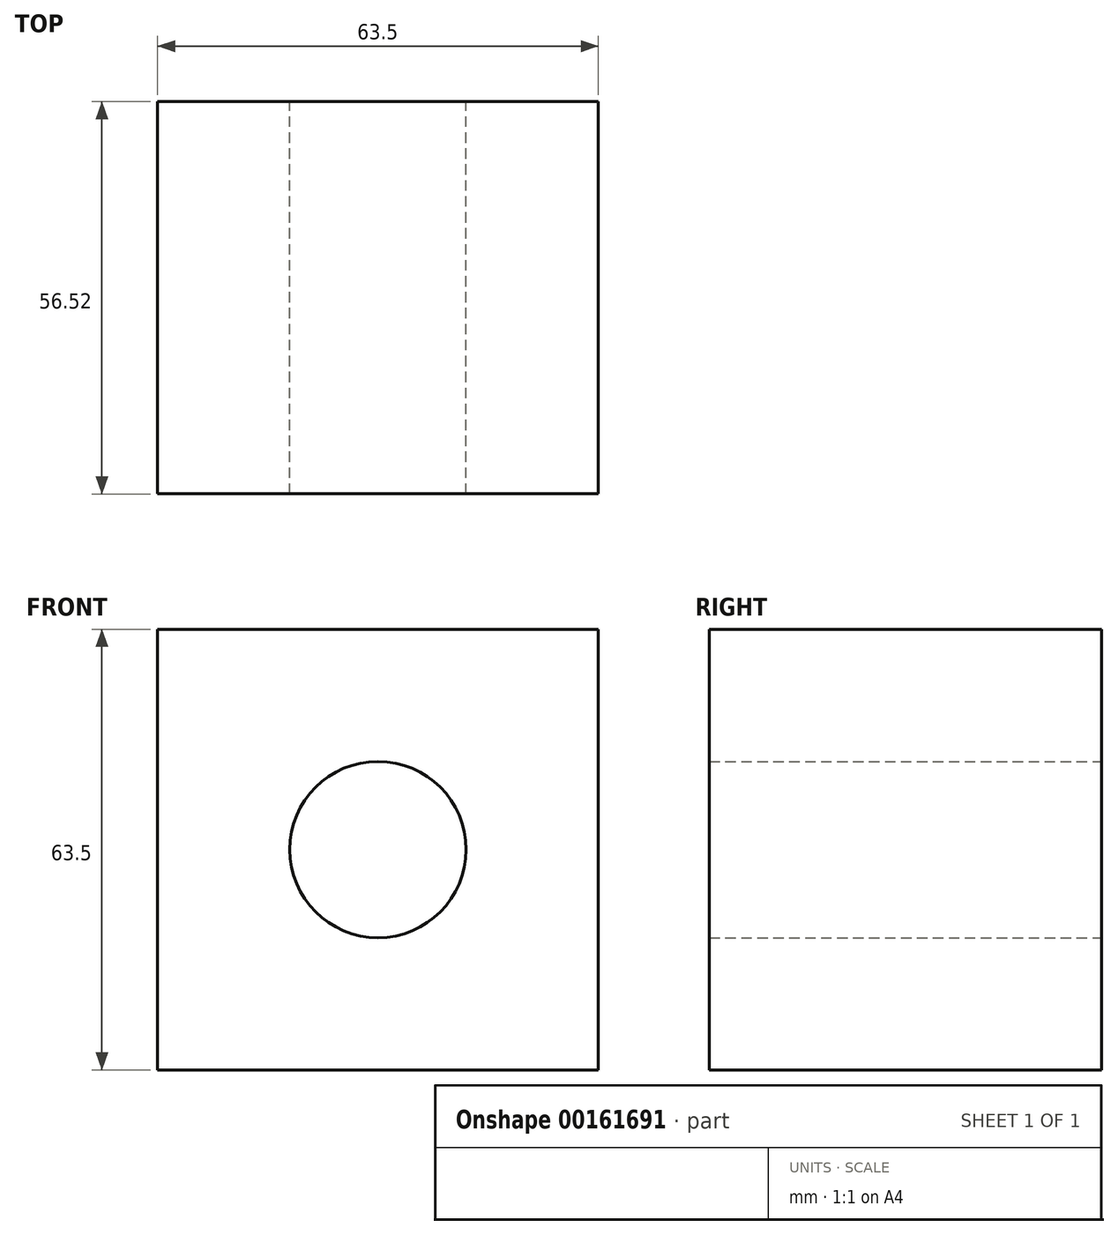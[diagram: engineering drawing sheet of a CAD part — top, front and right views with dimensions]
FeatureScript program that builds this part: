
annotation { "Feature Type Name" : "Feature", "Feature Type Description" : "" }
export const myFeature = defineFeature(function(context is Context, id is Id, definition is map)
    precondition{}
    {
        {
            var Q0;
            Q0=qCreatedBy(makeId("Front.planeOp"),FACE);
            var sketch = newSketch(context, id + "F0", { "sketchPlane" : qUnion([Q0])});
            skCircle(sketch, "E0", {"center": v(0, 0) * mm, "radius": 12.7 * mm});
            skCircle(sketch, "E1", {"center": v(0, 0) * mm, "radius": 31.75 * mm});
            skLineSegment(sketch, "E2.bottom", {"start": v(-31.75, 31.75) * mm, "end": v(31.75, 31.75) * mm});
            skLineSegment(sketch, "E2.top", {"start": v(-31.75, -31.75) * mm, "end": v(31.75, -31.75) * mm});
            skLineSegment(sketch, "E2.left", {"start": v(-31.75, 31.75) * mm, "end": v(-31.75, -31.75) * mm});
            skLineSegment(sketch, "E2.right", {"start": v(31.75, 31.75) * mm, "end": v(31.75, -31.75) * mm});
            skSolve(sketch);
        }
        {
            var Q0;
            Q0 = qSketchRegion(id + "F0", true);
            extrude(context, id + "F1", {"entities" : qUnion([Q0]), "depth" : 56.52 * mm});
        }
    });
